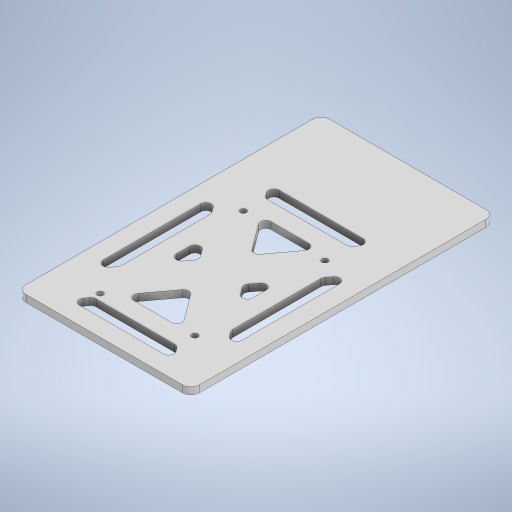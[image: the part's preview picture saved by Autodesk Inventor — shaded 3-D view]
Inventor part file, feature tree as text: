
AUTODESK INVENTOR PART (.ipt)
format: ipt  version: 2023 (Build 270158000, 158)  size: 402,944 bytes
history: native  units: in
note: dims shown in document units (in); Inventor stores cm internally (conversion verified against a paired STEP export)
features: sketch x3, extrude x2, fillet x2, hole x1, thicken_offset x1
ambient origin geometry x8: Origin, YZ Plane, XZ Plane, XY Plane, X Axis, Y Axis, Z Axis, Center Point
bodies: Solid1 (feature_tree)
feature tree (9):
  extrude  "Extrusion1"  Depth=3.937in
  hole  "Hole1"  [1 undecoded]
  extrude  "Extrusion3"  Depth=0.3937in
  thicken_offset  "Thicken1"
  fillet  "Fillet4"  Radius=0.3937in
  fillet  "Fillet5"  Radius=0.3937in
  sketch  "Sketch1"  dims[d0=5.315in d1=3.937in]
  sketch  "Sketch3"  dims[d2=0.1575in d3=0.0in d11=2.1in]
  sketch  "Sketch4"  dims[d18=0.1339in d19=0.2362in d20=0.248in d21=0.0787in d22=90.0deg d23=0.315in d24=0.8108in d27=0.3937in d29=0.3937in d30=0.3937in d31=0.3937in d32=0.3937in d33=0.3937in d34=0.0in d35=0.0in d40=0.55in d42=4.0in d48=0.1in d49=0.6in d50=0.0993in d51=1.5748in d52=1.5748in d53=0.1969in d56=3.55in d57=3.8in d58=0.315in d59=0.315in d60=0.1181in]
note: 1 required parameter value undecoded (feature->parameter linkage not recoverable at this tier; creation-order binding heuristic only, values carry confidence <= 0.55)
